# Revit family: Cortadora_CA-4V_1_GENERADO
name_source: partatom
category: Equipos especializados
units: mm (PartAtom-declared; Revit-internal decimal feet)

## family parameters
Compartido = No
Corte con vacíos al cargar = No
Cota de conector redondo = Diámetro de uso
Número OmniClass = 23.21.21.31.19.11
Punto de cálculo de habitación = No
Se basa en plano de trabajo = No
Siempre vertical = Sí
Tipo de pieza = Normal

## types (3) — shared parameters
Comentarios de tipo = High-production commercial vegetable preparation machine, up to 650 Kg.
Depth = 400 mm  [stored 1.31234 ft]
Fabricante = SAMMIC S.L.
Foodservice Equipment Identifier = Sí
Height = 652 mm  [stored 2.13911 ft]
Revision Code = 1
Specification by Manufacturer = Variable speed motor block + high-production head.
Equipped with "brushless" technology.
URL = https://www.sammic.com
URL Cutsheet = http://www.sammic.com
Weight in Pounds = 59.5
Width = 391 mm  [stored 1.28281 ft]
zero-valued in all types: Elevación por defecto

## per-type parameters (varying)
| type | Conn Plug | Cycle | FL Amps | HP | Modelo | Phase | Volts | Watts |
| Vegetable preparation machine CA-4V 230/50-60/1 | EU (SCHUKO 2P+G) | 50 Hz | 10 A | 2.01 | 1050796 | 1 | 230 V | 1500 W |
| Vegetable preparation machine CA-4V 120/50-60/1 | USA (NEMA 5-15P / 2P+G) | 60 Hz | 15 A |  | 1050799 | 1 | 120 V | 0 W |
| Vegetable preparation machine CA-4V 230/50-60/1 KSA |  | 0 Hz | 0 A | 2.01 | 1050765 | 0 | 0 V | 1500 W |

note: column(s) folded — value = type name in every type: Descripción

note: [stored X ft] marks values corroborated as IEEE doubles in the binary element streams (Revit-internal decimal feet)
